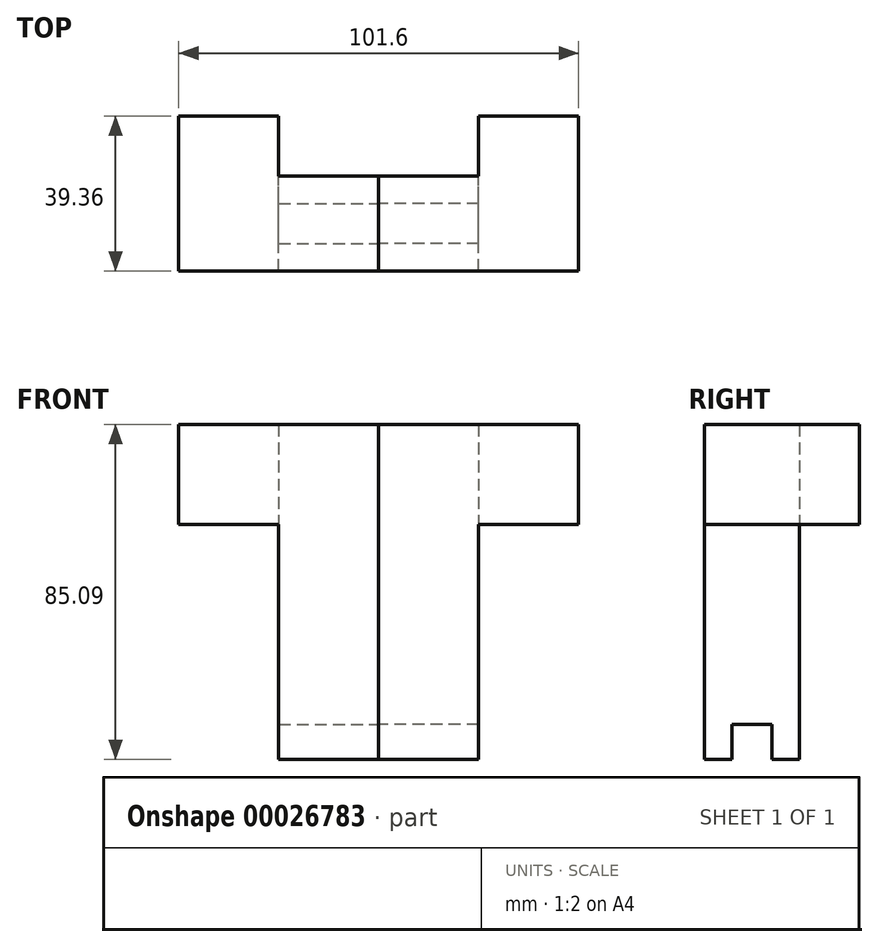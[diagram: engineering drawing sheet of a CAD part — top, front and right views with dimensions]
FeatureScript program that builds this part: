
annotation { "Feature Type Name" : "Feature", "Feature Type Description" : "" }
export const myFeature = defineFeature(function(context is Context, id is Id, definition is map)
    precondition{}
    {
        {
            var Q0;
            Q0=qCreatedBy(makeId("Top.planeOp"),FACE);
            var sketch = newSketch(context, id + "F0", { "sketchPlane" : qUnion([Q0])});
            skLineSegment(sketch, "E0.rect.bottom", {"start": v(12.7, -12.07) * mm, "end": v(-12.7, -12.07) * mm});
            skLineSegment(sketch, "E0.rect.top", {"start": v(12.7, 12.07) * mm, "end": v(-12.7, 12.07) * mm});
            skLineSegment(sketch, "E0.rect.left", {"start": v(12.7, -12.07) * mm, "end": v(12.7, 12.06) * mm});
            skLineSegment(sketch, "E0.rect.right", {"start": v(-12.7, -12.06) * mm, "end": v(-12.7, 12.07) * mm});
            skPoint(sketch, "E0.rect.middle", {"position": v(0, 0) * mm});
            skLineSegment(sketch, "E1.rect.bottom", {"start": v(12.7, -5.08) * mm, "end": v(-12.7, -5.08) * mm});
            skLineSegment(sketch, "E1.rect.top", {"start": v(12.7, 5.08) * mm, "end": v(-12.7, 5.08) * mm});
            skLineSegment(sketch, "E1.rect.left", {"start": v(12.7, -5.08) * mm, "end": v(12.7, 5.08) * mm});
            skLineSegment(sketch, "E1.rect.right", {"start": v(-12.7, -5.08) * mm, "end": v(-12.7, 5.08) * mm});
            skSolve(sketch);
        }
        {
            var Q0;
            Q0 = qSketchRegion(id + "F0", true);
            extrude(context, id + "F1", {"entities" : qUnion([Q0]), "depth" : 50.8 * mm});
        }
        {
            var Q0;
            {var subQ2=sQuery(id+"F0.wireOp",EDGE,"E0.rect.bottom");Q0=makeQuery(id+"F0.imprint","IMPRINT",FACE,{"disambiguationData":[TD([[makeQuery(id+"F0.imprint","IMPRINT",EDGE,{"derivedFrom":subQ2}),-1.0]])]});}
            var Q1;
            {var subQ2=sQuery(id+"F0.wireOp",EDGE,"E0.rect.top");Q1=makeQuery(id+"F0.imprint","IMPRINT",FACE,{"disambiguationData":[TD([[makeQuery(id+"F0.imprint","IMPRINT",EDGE,{"derivedFrom":subQ2}),1.0]])]});}
            extrude(context, id + "F2", {"entities" : qUnion([Q0, Q1]), "operationType" : NewBodyOperationType.ADD, "oppositeDirection" : true, "depth" : 8.9 * mm});
        }
        {
            var Q0;
            Q0=makeQuery(id+"F1.opExtrude","CAP_FACE",FACE,{"disambiguationData":[OSD([sQuery(id+"F0.wireOp",EDGE,"E0.rect.bottom"),sQuery(id+"F0.wireOp",EDGE,"E0.rect.top"),sQuery(id+"F0.wireOp",EDGE,"E0.rect.left"),sQuery(id+"F0.wireOp",EDGE,"E0.rect.right"),sQuery(id+"F0.wireOp",EDGE,"E1.rect.left"),sQuery(id+"F0.wireOp",EDGE,"E1.rect.right")])],"isStart":false});
            var sketch = newSketch(context, id + "F3", { "sketchPlane" : qUnion([Q0])});
            skLineSegment(sketch, "E2.bottom", {"start": v(-12.7, 12.07) * mm, "end": v(38.1, 12.07) * mm});
            skLineSegment(sketch, "E2.top", {"start": v(-12.7, -12.07) * mm, "end": v(38.1, -12.07) * mm});
            skLineSegment(sketch, "E2.left", {"start": v(-12.7, 12.07) * mm, "end": v(-12.7, -12.07) * mm});
            skLineSegment(sketch, "E2.right", {"start": v(38.1, 12.07) * mm, "end": v(38.1, -12.07) * mm});
            skLineSegment(sketch, "E3.bottom", {"start": v(38.1, 12.07) * mm, "end": v(12.7, 12.07) * mm});
            skLineSegment(sketch, "E3.top", {"start": v(38.1, 27.3) * mm, "end": v(12.7, 27.3) * mm});
            skLineSegment(sketch, "E3.left", {"start": v(38.1, 12.07) * mm, "end": v(38.1, 27.3) * mm});
            skLineSegment(sketch, "E3.right", {"start": v(12.7, 12.07) * mm, "end": v(12.7, 27.3) * mm});
            skSolve(sketch);
        }
        {
            var Q0;
            Q0 = qSketchRegion(id + "F3", true);
            extrude(context, id + "F4", {"entities" : qUnion([Q0]), "operationType" : NewBodyOperationType.ADD, "depth" : 25.4 * mm});
        }
        {
            var Q0;
            Q0=makeQuery(id+"F1.opExtrude","SWEPT_BODY",BODY,{"disambiguationData":[OSD([sQuery(id+"F0.wireOp",EDGE,"E0.rect.bottom"),sQuery(id+"F0.wireOp",EDGE,"E0.rect.top"),sQuery(id+"F0.wireOp",EDGE,"E0.rect.left"),sQuery(id+"F0.wireOp",EDGE,"E0.rect.right"),sQuery(id+"F0.wireOp",EDGE,"E1.rect.left"),sQuery(id+"F0.wireOp",EDGE,"E1.rect.right")])]});
            var Q1;
            Q1=makeQuery(id+"F4.opExtrude","SWEPT_FACE",FACE,{"disambiguationData":[OSD([sQuery(id+"F3.wireOp",EDGE,"E3.top")])]});
            mirror(context, id + "F5", {"entities" : qUnion([Q0]), "mirrorPlane" : qUnion([Q1])});
        }
        {
            var Q0;
            Q0=makeQuery(id+"F5.opPattern","COPY",BODY,{"derivedFrom":makeQuery(id+"F1.opExtrude","SWEPT_BODY",BODY,{"disambiguationData":[OSD([sQuery(id+"F0.wireOp",EDGE,"E0.rect.bottom"),sQuery(id+"F0.wireOp",EDGE,"E0.rect.top"),sQuery(id+"F0.wireOp",EDGE,"E0.rect.left"),sQuery(id+"F0.wireOp",EDGE,"E0.rect.right"),sQuery(id+"F0.wireOp",EDGE,"E1.rect.left"),sQuery(id+"F0.wireOp",EDGE,"E1.rect.right")])]}),"instanceName":"1"});
            deleteBodies(context, id + "F6", {"entities" : qUnion([Q0])});
        }
        {
            var Q0;
            Q0=makeQuery(id+"F1.opExtrude","SWEPT_BODY",BODY,{"disambiguationData":[OSD([sQuery(id+"F0.wireOp",EDGE,"E0.rect.bottom"),sQuery(id+"F0.wireOp",EDGE,"E0.rect.top"),sQuery(id+"F0.wireOp",EDGE,"E0.rect.left"),sQuery(id+"F0.wireOp",EDGE,"E0.rect.right"),sQuery(id+"F0.wireOp",EDGE,"E1.rect.left"),sQuery(id+"F0.wireOp",EDGE,"E1.rect.right")])]});
            var Q1;
            {var subQ0=sQuery(id+"F0.wireOp",EDGE,"E0.rect.right");var subQ1=sQuery(id+"F0.wireOp",EDGE,"E1.rect.right");Q1=makeQuery(id+"F4.boolean.opBoolean","MERGE",FACE,{"derivedFrom":[makeQuery(id+"F2.boolean.opBoolean","MERGE",FACE,{"derivedFrom":[makeQuery(id+"F1.opExtrude","SWEPT_FACE",FACE,{"disambiguationData":[OSD([subQ0,subQ1])]}),makeQuery(id+"F2.opExtrude","SWEPT_FACE",FACE,{"disambiguationData":[OSD([subQ0]),TDD([makeQuery(id+"F0.imprint","IMPRINT",EDGE,{"disambiguationData":[TD([[makeQuery(id+"F0.imprint","INTERSECT",VERTEX,{"derivedFrom":[sQuery(id+"F0.wireOp",EDGE,"E0.rect.bottom"),subQ0]}),-1.0]])],"derivedFrom":subQ0})])]}),makeQuery(id+"F2.opExtrude","SWEPT_FACE",FACE,{"disambiguationData":[OSD([subQ0]),TDD([makeQuery(id+"F0.imprint","IMPRINT",EDGE,{"disambiguationData":[TD([[makeQuery(id+"F0.imprint","INTERSECT",VERTEX,{"derivedFrom":[sQuery(id+"F0.wireOp",EDGE,"E0.rect.top"),subQ0]}),1.0]])],"derivedFrom":subQ0})])]})]}),makeQuery(id+"F4.opExtrude","SWEPT_FACE",FACE,{"disambiguationData":[OSD([sQuery(id+"F3.wireOp",EDGE,"E2.left")])]})]});}
            mirror(context, id + "F7", {"entities" : qUnion([Q0]), "mirrorPlane" : qUnion([Q1])});
        }
    });
